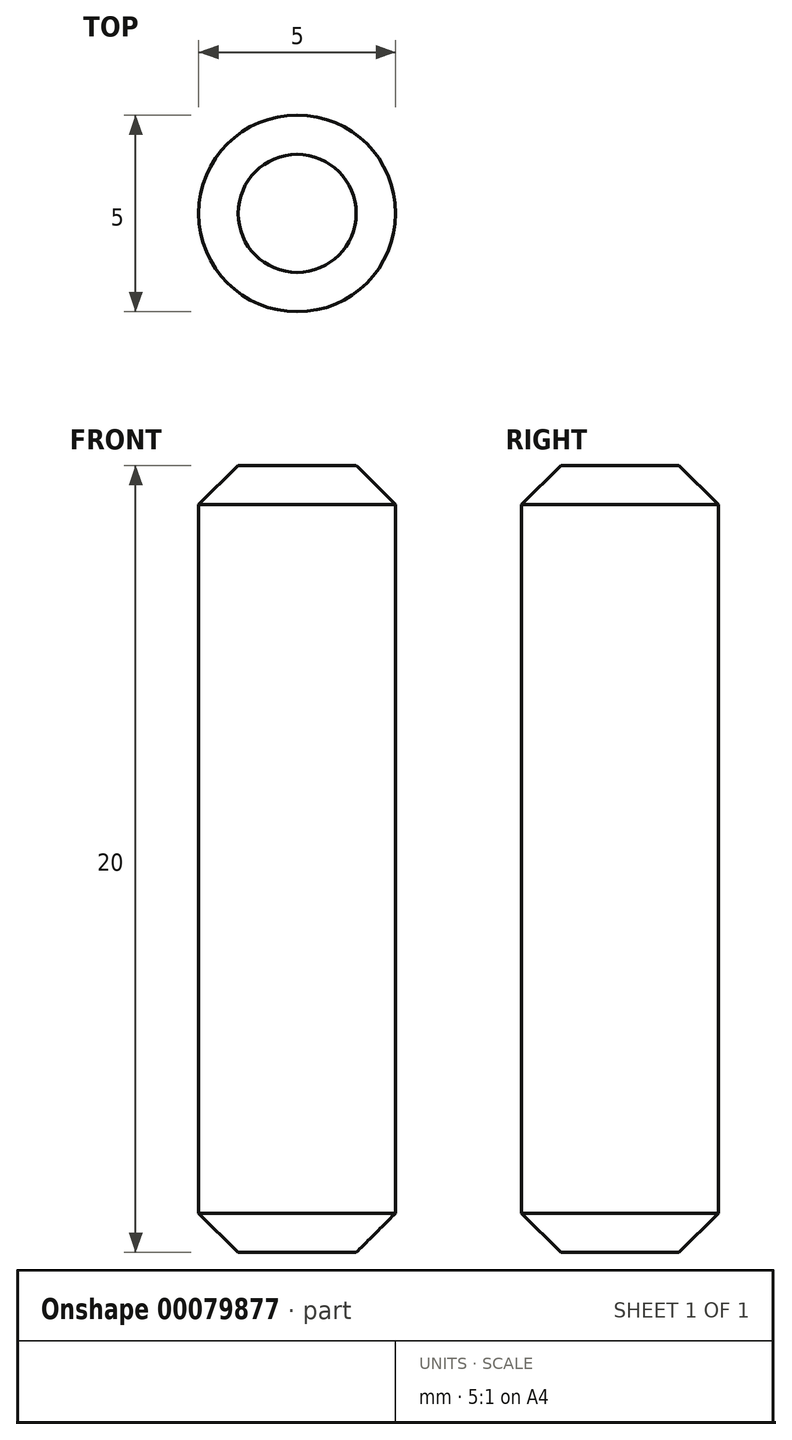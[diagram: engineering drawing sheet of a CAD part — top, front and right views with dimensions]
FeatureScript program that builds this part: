
annotation { "Feature Type Name" : "Feature", "Feature Type Description" : "" }
export const myFeature = defineFeature(function(context is Context, id is Id, definition is map)
    precondition{}
    {
        {
            assignVariable(context, id + "F0", {"name" : "pin_length", "anyValue" : 20});
        }
        {
            var Q0;
            Q0=qCreatedBy(makeId("Top.planeOp"),FACE);
            var sketch = newSketch(context, id + "F1", { "sketchPlane" : qUnion([Q0])});
            skCircle(sketch, "E0", {"center": v(0, 0) * mm, "radius": 2.5 * mm});
            skSolve(sketch);
        }
        {
            var Q0;
            Q0 = qSketchRegion(id + "F1", true);
            extrude(context, id + "F2", {"entities" : qUnion([Q0]), "endBound" : BoundingType.SYMMETRIC, "depth" : (getVariable(context, 'pin_length')) * mm});
        }
        {
            var Q0;
            Q0=makeQuery(id+"F2.opExtrude","CAP_EDGE",EDGE,{"disambiguationData":[OSD([sQuery(id+"F1.wireOp",EDGE,"E0")])],"isStart":false});
            var Q1;
            Q1=makeQuery(id+"F2.opExtrude","CAP_EDGE",EDGE,{"disambiguationData":[OSD([sQuery(id+"F1.wireOp",EDGE,"E0")])],"isStart":true});
            chamfer(context, id + "F3", {"entities" : qUnion([Q0, Q1]), "width" : 1 * mm, "tangentPropagation" : true});
        }
    });
